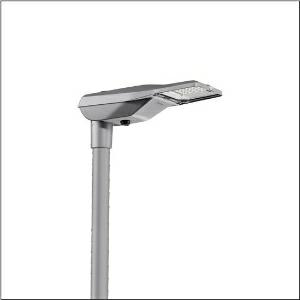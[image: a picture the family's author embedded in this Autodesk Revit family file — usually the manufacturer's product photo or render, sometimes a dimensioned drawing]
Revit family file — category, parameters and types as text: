
# Revit family: streetlight_sl_21_iq_micro___st1_0a_5xe1d31u08db_5c5a
name_source: partatom
category: Lighting Fixtures
units: mm (PartAtom-declared; Revit-internal decimal feet)

## family parameters
Cut with Voids When Loaded = No
Host = Face
Light Source = No
Part Type = Normal
Room Calculation Point = No
Round Connector Dimension = Use Diameter
Shared = No

## types (1)
- --- (1 x LED, 5110 lm, 39.1 W, 3000K)
    Apparent Load = 39 VA
    CIE Flux Codes = 37 72 97 100 100
    Color Rendering = 70
    Color Temperature = 3000K
    Default Elevation = 1800 mm
    Description = Streetlight SL 21 iQ micro, mast luminaire, primary light control with lens, of PMMA, primary optical cover: cover, of toughened safety glass, transparent, light distribution: ST1.0a, light emission: direct distribution, primary light characteristic: asymmetric, installation type: post-top, side-entry, LED, High Power LED, rated luminous flux: 5.110lm, luminous efficacy: 131lm/W, light colour: 730, colour temperature: 3000K, control gear: iQ-Street Remote, D4i with power reduction, control: pre-setting: logarithmic dimming characteristic, Street-Remote, Auto-Match, Temp-Guard, Lumen-Switch, Night-Set, Smart-Wire, Light-Fading, Desk-Remote (wireless, voltage-free reading and setting of iQ features in the workshop via application-optimized NFC function/RFID function), optimised constant luminous flux control (CLO 2.0), mains connection: 220..240V, AC, 50/60Hz, start of lifetime: 39W, end of service life: 41W, reduction: 17W, luminaire housing, of diecast aluminium, powder-coated, SITECO metallic grey (DB 702S), corrosivity category C5 high according to DIN EN ISO 12944, please order mast flange separately, inclination adjustable: 0°, 5°, 10°, 15°, sealing non-destructively replaceable, multi-level sealing system, length: 528mm, width: 235mm, height: 110mm, mast flange for spigot size: 42mm (side-entry): 5XC10008XM4, 60/48mm (side-entry/post-top): 5XC10108XM2, 76/60mm (side-entry/post-top): 5XC10108XM1, mounting height: 4..8m, Smart Interface below, protection rating (complete): IP66, insulation class (complete): insulation class II (safety insulation), certification: CE, ENEC, ENEC+, VDE, impact resistance: IK10, permissible operating ambient temperature for outdoor applications: -40..+50°C, standard-compliant lighting for roads and squares, packaging unit: 1 piece

Light Distribution: ST1.0a
    Height = 110 mm
    Lamp = 1 x LED
    Lamp Light Flux = 5110 lm
    Lamp Power = 39.1 W
    Lamp count = 1
    Length = 528 mm
    Luminous efficacy = 131 lm/W
    Manufacturer = Siteco
    ModVariant = No
    Model = 5XE1D31U08DB
    Number of Poles = 1
    OnlyDefault = Yes
    Power Factor = 1
    Product Name = Streetlight SL 21 iQ micro | ST1.0a
    Product group = mast luminaire | pylon top
    ProductGroupID = 6100
    Protection Class = Protection class II
    Protection Degree = IP 66
    RLX_Detail_Level = 1
    RLX_Emergency_Light_Flux = 0 lm
    RLX_Emergency_Type = 0
    RLX_Emergency_Type_DB = No
    RlxData = <blob elided: 99221 chars, md5=4d646e4f>
    Socket = socket
    Standby Power = 0 W
    System Light Flux = 5110 lm
    System Power = 39 W
    Type Comments = factory setting: luminous flux: 100 % | dim-lin: 254 | 765 mA
    Type Image = l_1277290.jpg
    URL = http://relux.com
    VarID = @adj_115845
    Voltage = 0 V
    Weight = 0.00 kg
    Width = 235 mm

## geometry (parser evidence)
native form markers: Blend x4, Sweep x9
no freeform markers — native parametric forms only
